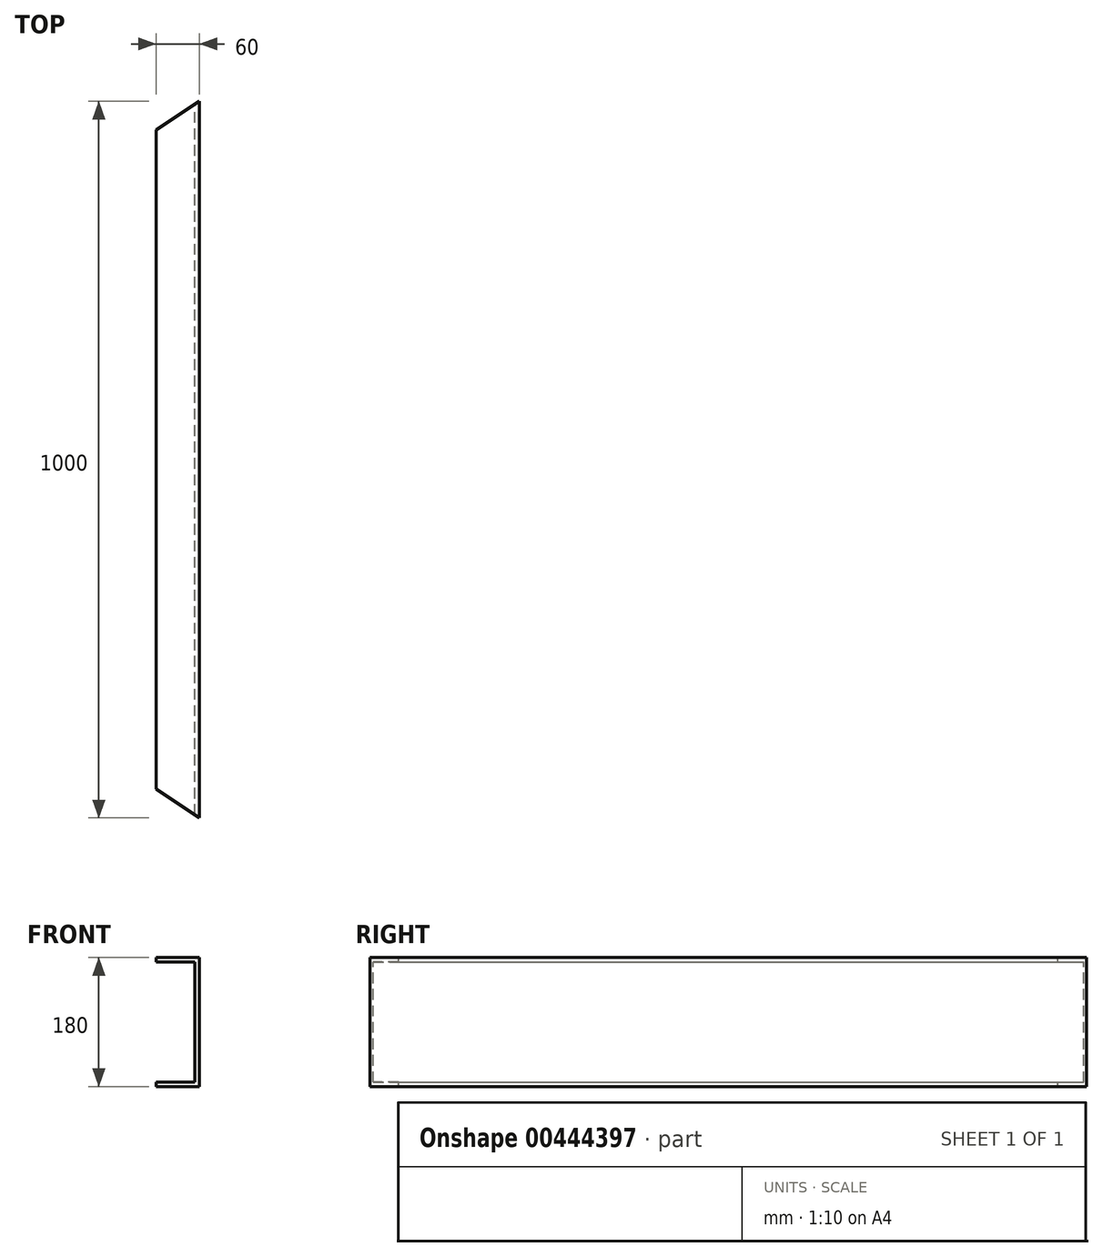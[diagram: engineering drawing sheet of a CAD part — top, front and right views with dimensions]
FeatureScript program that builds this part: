
annotation { "Feature Type Name" : "Feature", "Feature Type Description" : "" }
export const myFeature = defineFeature(function(context is Context, id is Id, definition is map)
    precondition{}
    {
        {
            var Q0;
            Q0=qCreatedBy(makeId("Front.planeOp"),FACE);
            var sketch = newSketch(context, id + "F0", { "sketchPlane" : qUnion([Q0])});
            skLineSegment(sketch, "E0.bottom", {"start": v(0, 0) * mm, "end": v(60, 0) * mm});
            skLineSegment(sketch, "E0.top", {"start": v(0, 180) * mm, "end": v(60, 180) * mm});
            skLineSegment(sketch, "E0.left", {"start": v(0, 0) * mm, "end": v(0, 6) * mm});
            skLineSegment(sketch, "E0.right", {"start": v(60, 0) * mm, "end": v(60, 180) * mm});
            skLineSegment(sketch, "E1.1", {"start": v(0, 6) * mm, "end": v(54, 6) * mm});
            skLineSegment(sketch, "E1.2", {"start": v(54, 6) * mm, "end": v(54, 174) * mm});
            skLineSegment(sketch, "E1.3", {"start": v(0, 174) * mm, "end": v(54, 174) * mm});
            skLineSegment(sketch, "E2.trimOffspring", {"start": v(0, 174) * mm, "end": v(0, 180) * mm});
            skSolve(sketch);
        }
        {
            var Q0;
            Q0 = qSketchRegion(id + "F0", true);
            extrude(context, id + "F1", {"entities" : qUnion([Q0]), "depth" : 1000 * mm});
        }
        {
            var Q0;
            Q0=makeQuery(id+"F1.opExtrude","SWEPT_FACE",FACE,{"disambiguationData":[OSD([sQuery(id+"F0.wireOp",EDGE,"E0.top")])]});
            var sketch = newSketch(context, id + "F2", { "sketchPlane" : qUnion([Q0])});
            skLineSegment(sketch, "E3", {"start": v(0, -500) * mm, "end": v(266.44, -500) * mm});
            skLineSegment(sketch, "E4", {"start": v(0, 0) * mm, "end": v(60, 0) * mm});
            skLineSegment(sketch, "E5.MirrorCS", {"start": v(0, -1000) * mm, "end": v(60, -1000) * mm});
            skLineSegment(sketch, "E6", {"start": v(0, 0) * mm, "end": v(0, -40) * mm});
            skLineSegment(sketch, "E7", {"start": v(0, -40) * mm, "end": v(60, 0) * mm});
            skLineSegment(sketch, "E8", {"start": v(0, -1000) * mm, "end": v(0, -960) * mm});
            skLineSegment(sketch, "E9", {"start": v(0, -960) * mm, "end": v(60, -1000) * mm});
            skSolve(sketch);
        }
        {
            var Q0;
            Q0=makeQuery(id+"F2.imprint","IMPRINT",FACE,{"disambiguationData":[TD([[makeQuery(id+"F2.imprint","IMPRINT",EDGE,{"derivedFrom":sQuery(id+"F2.wireOp",EDGE,"E5.MirrorCS")}),1.0]])]});
            var Q1;
            Q1=makeQuery(id+"F2.imprint","IMPRINT",FACE,{"disambiguationData":[TD([[makeQuery(id+"F2.imprint","IMPRINT",EDGE,{"derivedFrom":sQuery(id+"F2.wireOp",EDGE,"E4")}),-1.0]])]});
            extrude(context, id + "F3", {"entities" : qUnion([Q0, Q1]), "operationType" : NewBodyOperationType.REMOVE, "endBound" : BoundingType.THROUGH_ALL, "oppositeDirection" : true, "depth" : 25 * mm});
        }
    });
